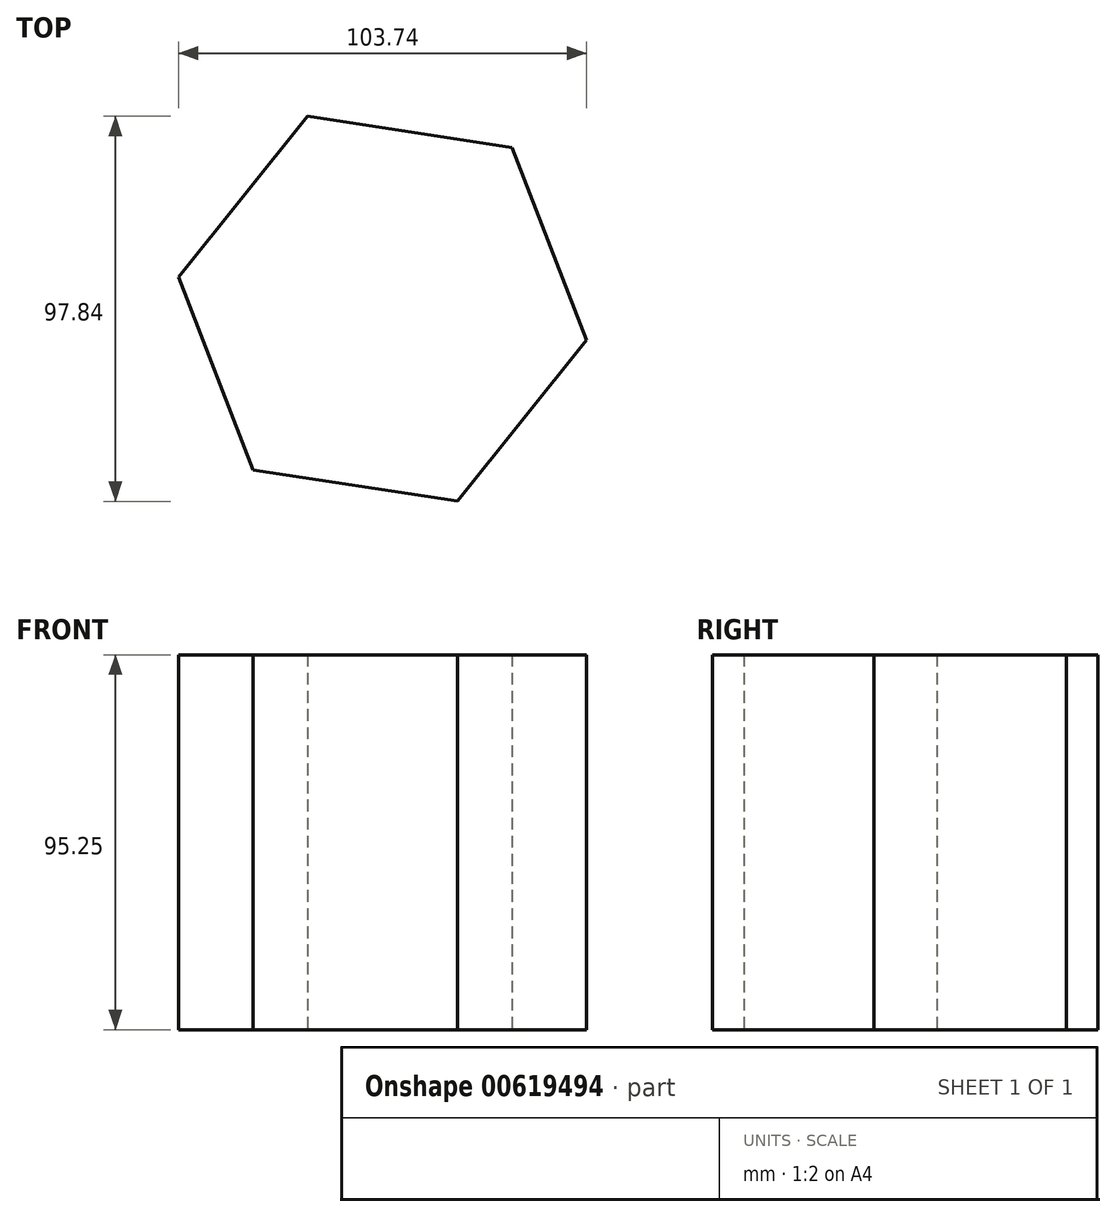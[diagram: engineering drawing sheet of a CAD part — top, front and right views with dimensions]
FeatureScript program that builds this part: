
annotation { "Feature Type Name" : "Feature", "Feature Type Description" : "" }
export const myFeature = defineFeature(function(context is Context, id is Id, definition is map)
    precondition{}
    {
        {
            var Q0;
            Q0=qCreatedBy(makeId("Top.planeOp"),FACE);
            var sketch = newSketch(context, id + "F0", { "sketchPlane" : qUnion([Q0])});
            skCircle(sketch, "E0.cCircle", {"center": v(0, 0) * mm, "radius": 45.45 * mm, "construction": true});
            skLineSegment(sketch, "E0.0", {"start": v(-51.87, 8) * mm, "end": v(-19, 48.92) * mm});
            skLineSegment(sketch, "E0.1", {"start": v(-19, 48.92) * mm, "end": v(32.86, 40.92) * mm});
            skLineSegment(sketch, "E0.2", {"start": v(32.86, 40.92) * mm, "end": v(51.87, -8) * mm});
            skLineSegment(sketch, "E0.3", {"start": v(51.87, -8) * mm, "end": v(19, -48.92) * mm});
            skLineSegment(sketch, "E0.4", {"start": v(19, -48.92) * mm, "end": v(-32.86, -40.92) * mm});
            skLineSegment(sketch, "E0.5", {"start": v(-32.86, -40.92) * mm, "end": v(-51.87, 8) * mm});
            skPoint(sketch, "E0.0.midPoint", {"position": v(-35.44, 28.46) * mm});
            skSolve(sketch);
        }
        {
            var Q0;
            Q0=makeQuery(id+"F0.imprint","IMPRINT",FACE,{"disambiguationData":[TD([[makeQuery(id+"F0.imprint","IMPRINT",EDGE,{"derivedFrom":sQuery(id+"F0.wireOp",EDGE,"E0.0")}),-1.0]])]});
            extrude(context, id + "F1", {"entities" : qUnion([Q0]), "depth" : 95.25 * mm, "offsetDistance" : 25.4 * mm});
        }
    });
